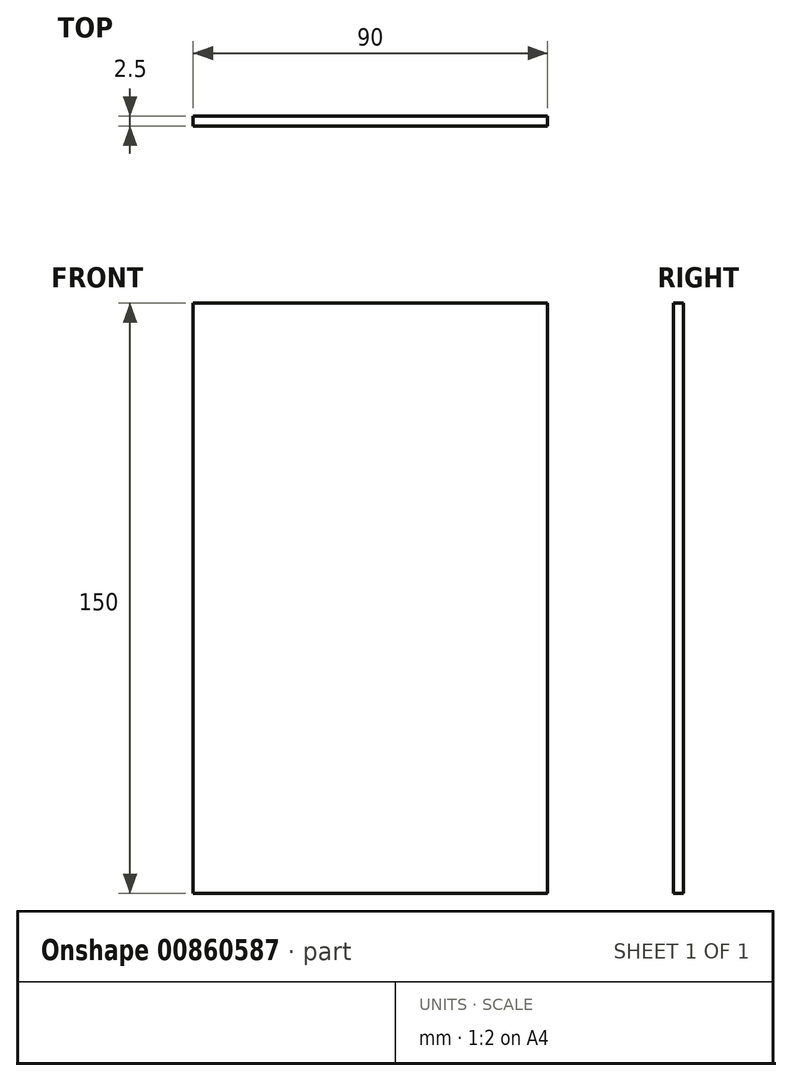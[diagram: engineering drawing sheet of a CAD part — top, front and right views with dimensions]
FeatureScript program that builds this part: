
annotation { "Feature Type Name" : "Feature", "Feature Type Description" : "" }
export const myFeature = defineFeature(function(context is Context, id is Id, definition is map)
    precondition{}
    {
        {
            var Q0;
            Q0=qCreatedBy(makeId("Front.planeOp"),FACE);
            var sketch = newSketch(context, id + "F0", { "sketchPlane" : qUnion([Q0])});
            skLineSegment(sketch, "E0.bottom", {"start": v(45, 75) * mm, "end": v(-45, 75) * mm});
            skLineSegment(sketch, "E0.top", {"start": v(45, -75) * mm, "end": v(-45, -75) * mm});
            skLineSegment(sketch, "E0.left", {"start": v(45, 75) * mm, "end": v(45, -75) * mm});
            skLineSegment(sketch, "E0.right", {"start": v(-45, 75) * mm, "end": v(-45, -75) * mm});
            skPoint(sketch, "E0.middle", {"position": v(0, 0) * mm});
            skSolve(sketch);
        }
        {
            var Q0;
            Q0 = qSketchRegion(id + "F0", true);
            extrude(context, id + "F1", {"entities" : qUnion([Q0]), "depth" : 2.5 * mm, "offsetDistance" : 25 * mm});
        }
    });
